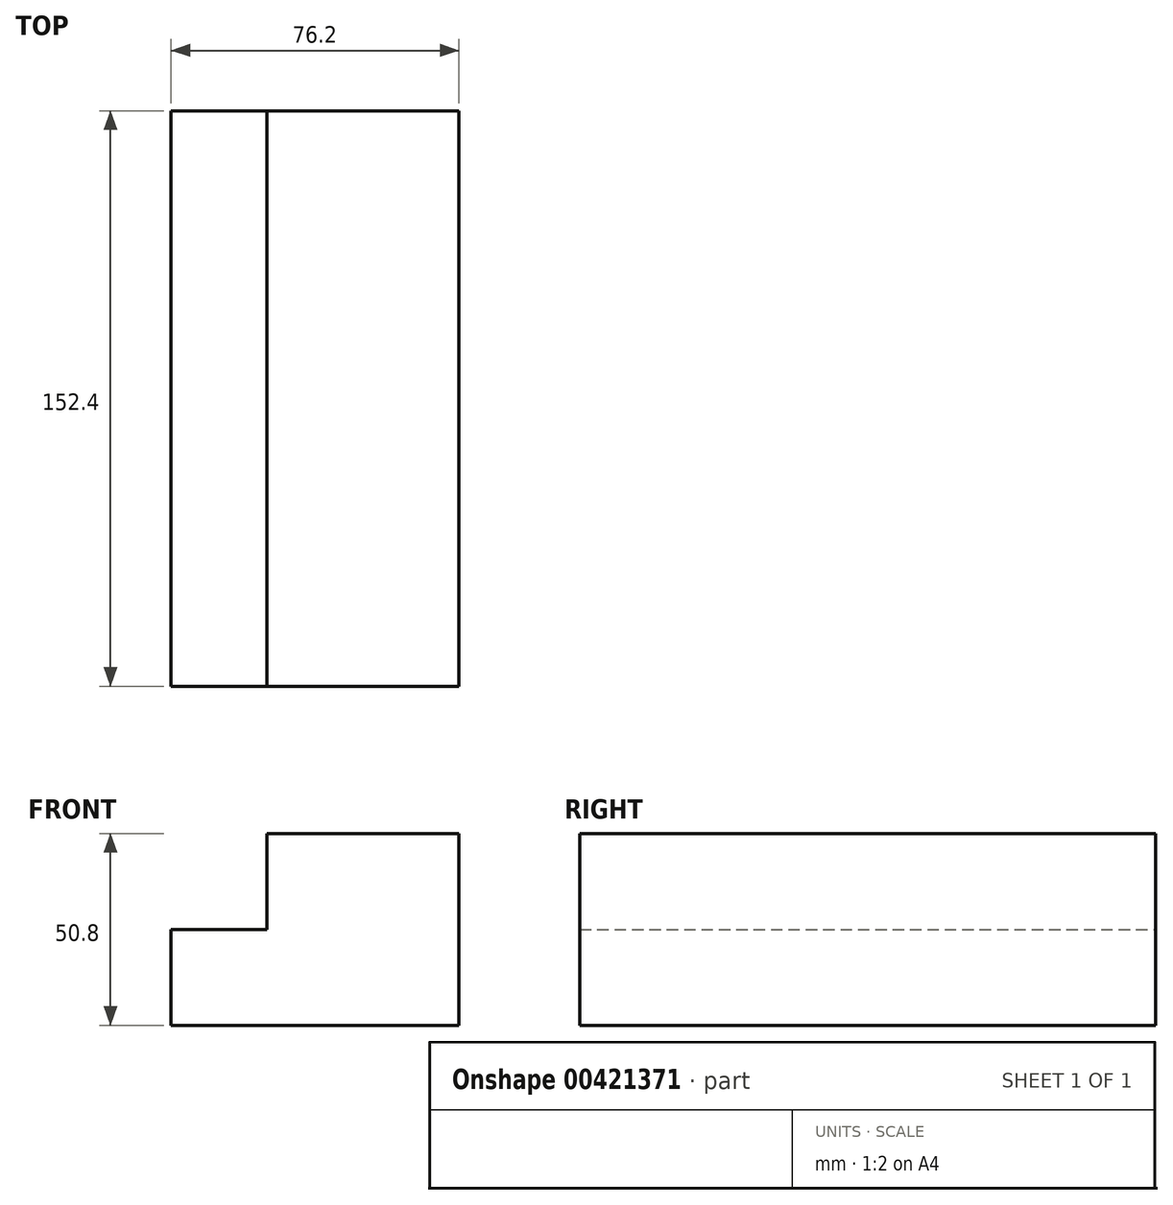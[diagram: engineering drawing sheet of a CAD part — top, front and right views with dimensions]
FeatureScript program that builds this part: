
annotation { "Feature Type Name" : "Feature", "Feature Type Description" : "" }
export const myFeature = defineFeature(function(context is Context, id is Id, definition is map)
    precondition{}
    {
        {
            var Q0;
            Q0=qCreatedBy(makeId("Front.planeOp"),FACE);
            var sketch = newSketch(context, id + "F0", { "sketchPlane" : qUnion([Q0])});
            skLineSegment(sketch, "E0", {"start": v(0, 0) * mm, "end": v(0, 25.4) * mm});
            skLineSegment(sketch, "E1", {"start": v(0, 25.4) * mm, "end": v(25.4, 25.4) * mm});
            skLineSegment(sketch, "E2", {"start": v(25.4, 25.4) * mm, "end": v(25.4, 50.8) * mm});
            skLineSegment(sketch, "E3", {"start": v(25.4, 50.8) * mm, "end": v(76.2, 50.8) * mm});
            skLineSegment(sketch, "E4", {"start": v(76.2, 50.8) * mm, "end": v(76.2, 0) * mm});
            skLineSegment(sketch, "E5", {"start": v(76.2, 0) * mm, "end": v(0, 0) * mm});
            skSolve(sketch);
        }
        {
            var Q0;
            Q0 = qSketchRegion(id + "F0", true);
            extrude(context, id + "F1", {"entities" : qUnion([Q0]), "depth" : 152.4 * mm});
        }
    });
